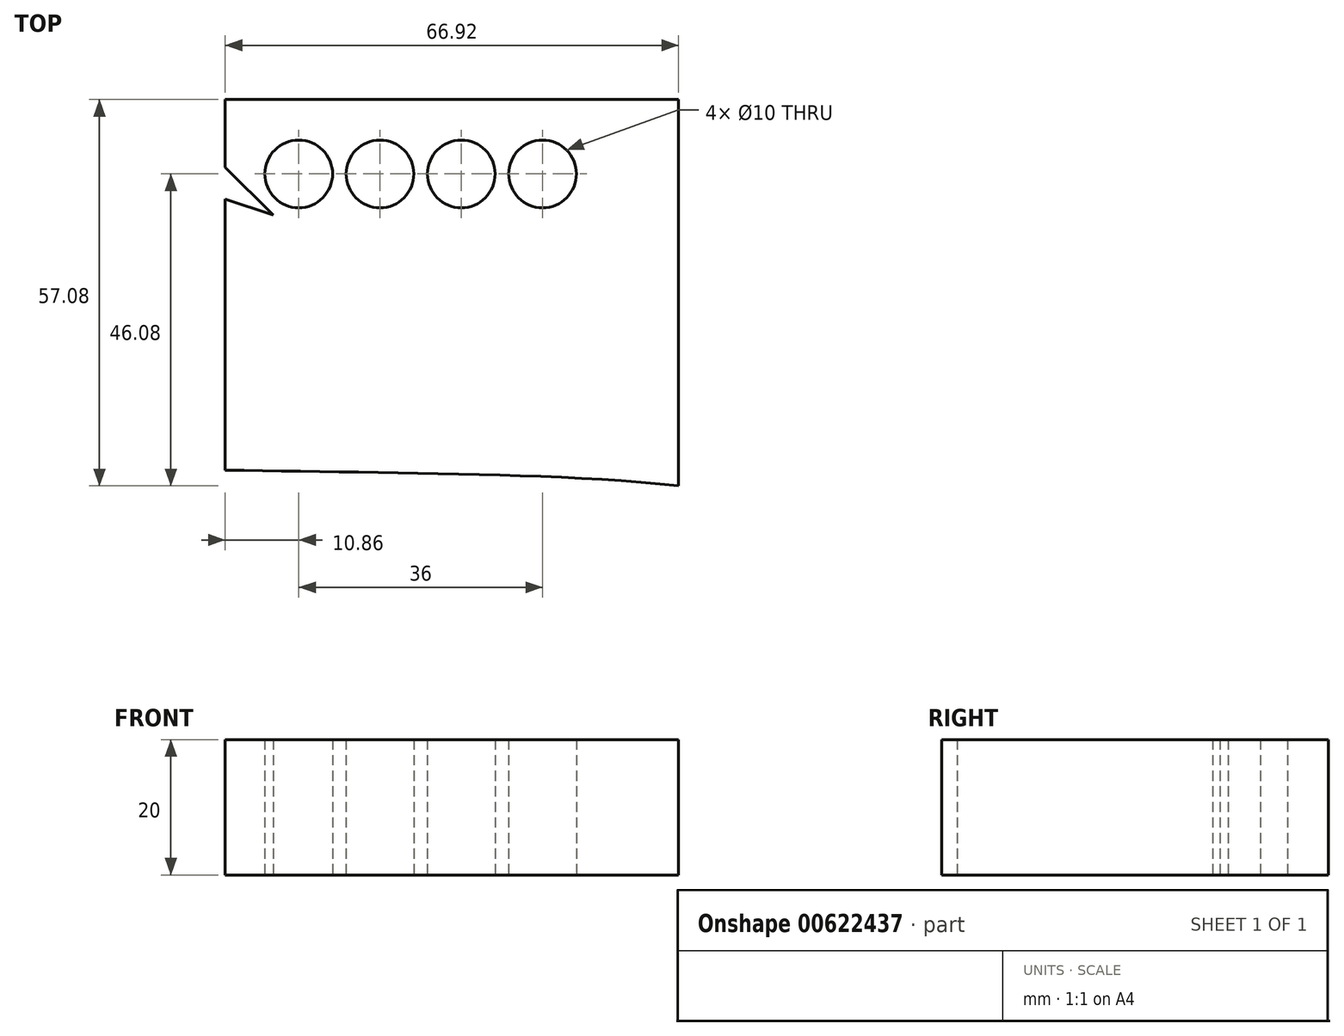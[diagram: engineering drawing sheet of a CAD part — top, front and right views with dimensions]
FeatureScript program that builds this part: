
annotation { "Feature Type Name" : "Feature", "Feature Type Description" : "" }
export const myFeature = defineFeature(function(context is Context, id is Id, definition is map)
    precondition{}
    {
        {
            var Q0;
            Q0=qCreatedBy(makeId("Top.planeOp"),FACE);
            var sketch = newSketch(context, id + "F0", { "sketchPlane" : qUnion([Q0])});
            skLineSegment(sketch, "E0", {"start": v(0, 0) * mm, "end": v(-230.94, 0) * mm});
            skLineSegment(sketch, "E1", {"start": v(-230.94, 0) * mm, "end": v(219.06, 0) * mm});
            skLineSegment(sketch, "E2", {"start": v(-178.77, 83.87) * mm, "end": v(166.23, 83.87) * mm});
            skLineSegment(sketch, "E3", {"start": v(-179.55, -84.3) * mm, "end": v(165.45, -84.3) * mm});
            skFitSpline(sketch, "E4", {"points": [v(-178.77, 83.87) * mm, v(-187.34, 83.87) * mm, v(-196.05, 82.03) * mm, v(-204.13, 75.85) * mm, v(-210.77, 67.6) * mm, v(-219.63, 55.04) * mm, v(-230.94, 0) * mm], "startDerivative": vector(-62.46, 1.75) * mm, "endDerivative": vector(-42.93, -222.96) * mm});
            skFitSpline(sketch, "E5", {"points": [v(-179.55, -84.3) * mm, v(-186, -84.3) * mm, v(-194.36, -82.98) * mm, v(-205.47, -75.53) * mm, v(-213.5, -67.51) * mm, v(-220.85, -55.02) * mm, v(-230.94, 0) * mm], "startDerivative": vector(-58.45, -0.77) * mm, "endDerivative": vector(-25.53, 220.68) * mm});
            skFitSpline(sketch, "E6", {"points": [v(79.72, -68.87) * mm, v(94.3, -68.2) * mm, v(121.52, -65.29) * mm, v(156.84, -57.83) * mm, v(194.43, -52) * mm, v(219.05, -51.68) * mm], "startDerivative": vector(92.48, 2.44) * mm, "endDerivative": vector(217.99, 5.07) * mm});
            skFitSpline(sketch, "E7.MirrorCS", {"points": [v(79.72, 68.87) * mm, v(94.3, 68.2) * mm, v(121.52, 65.29) * mm, v(156.84, 57.83) * mm, v(194.43, 52) * mm, v(219.05, 51.68) * mm], "startDerivative": vector(92.48, -2.44) * mm, "endDerivative": vector(217.99, -5.07) * mm});
            skLineSegment(sketch, "E8", {"start": v(219.05, -51.68) * mm, "end": v(219.05, 51.68) * mm});
            skFitSpline(sketch, "E9", {"points": [v(79.72, 68.87) * mm, v(56.8, 68.87) * mm, v(17.56, 68.87) * mm, v(-22.6, 68.87) * mm, v(-58.57, 65.44) * mm, v(-84.69, 58.45) * mm, v(-132, 55.24) * mm, v(-177.02, 54.67) * mm, v(-219.63, 55.04) * mm], "startDerivative": vector(-222.73, 0.47) * mm, "endDerivative": vector(-322.68, 5.5) * mm});
            skFitSpline(sketch, "E10.MirrorCS", {"points": [v(79.72, -68.87) * mm, v(56.8, -68.87) * mm, v(17.56, -68.87) * mm, v(-22.6, -68.87) * mm, v(-58.57, -65.44) * mm, v(-84.69, -58.45) * mm, v(-132, -55.24) * mm, v(-177.02, -54.67) * mm, v(-219.63, -55.04) * mm], "startDerivative": vector(-222.73, -0.47) * mm, "endDerivative": vector(-322.68, -5.5) * mm});
            skCircle(sketch, "E11", {"center": v(-150, 11) * mm, "radius": 5 * mm});
            skCircle(sketch, "E12", {"center": v(-138, 11) * mm, "radius": 5 * mm});
            skCircle(sketch, "E13", {"center": v(-126, 11) * mm, "radius": 5 * mm});
            skCircle(sketch, "E14", {"center": v(-114, 11) * mm, "radius": 5 * mm});
            skCircle(sketch, "E15.MirrorC", {"center": v(-150, -11) * mm, "radius": 5 * mm});
            skCircle(sketch, "E16.MirrorC", {"center": v(-138, -11) * mm, "radius": 5 * mm});
            skCircle(sketch, "E17.MirrorC", {"center": v(-126, -11) * mm, "radius": 5 * mm});
            skCircle(sketch, "E18.MirrorC", {"center": v(-114, -11) * mm, "radius": 5 * mm});
            skFitSpline(sketch, "E19", {"points": [v(-225.2, 0) * mm, v(-222.12, 3.4) * mm, v(-216.92, 6.48) * mm, v(-200.74, 8.98) * mm, v(-175.64, 9.89) * mm, v(-160.86, 10) * mm], "startDerivative": vector(24.07, 28.7) * mm, "endDerivative": vector(83.9, -2.27) * mm});
            skFitSpline(sketch, "E20.MirrorCS", {"points": [v(-225.2, 0) * mm, v(-222.12, -3.4) * mm, v(-216.92, -6.48) * mm, v(-200.74, -8.98) * mm, v(-175.64, -9.89) * mm, v(-160.86, -10) * mm], "startDerivative": vector(24.07, -28.7) * mm, "endDerivative": vector(83.9, 2.27) * mm});
            skLineSegment(sketch, "E21", {"start": v(-160.86, 10) * mm, "end": v(-153.79, 17.07) * mm});
            skLineSegment(sketch, "E22", {"start": v(-153.79, 17.07) * mm, "end": v(-175.64, 9.89) * mm});
            skLineSegment(sketch, "E23.MirrorCS", {"start": v(-153.79, -17.07) * mm, "end": v(-175.64, -9.89) * mm});
            skLineSegment(sketch, "E24.MirrorCS", {"start": v(-160.86, -10) * mm, "end": v(-153.79, -17.07) * mm});
            skLineSegment(sketch, "E25", {"start": v(-160.86, -10) * mm, "end": v(-160.86, 10) * mm});
            skFitSpline(sketch, "E26", {"points": [v(-178.77, 83.87) * mm, v(-169.02, 82.7) * mm, v(-159.87, 79.14) * mm, v(-148.12, 75.77) * mm, v(-129.24, 75.28) * mm, v(-93.94, 75.39) * mm, v(-67.97, 75) * mm], "startDerivative": vector(81.86, -4.03) * mm, "endDerivative": vector(119.84, 0.08) * mm});
            skFitSpline(sketch, "E27.MirrorCS", {"points": [v(-178.77, -83.87) * mm, v(-169.02, -82.7) * mm, v(-159.87, -79.14) * mm, v(-148.12, -75.77) * mm, v(-129.24, -75.28) * mm, v(-93.94, -75.39) * mm, v(-67.97, -75) * mm], "startDerivative": vector(81.86, 4.03) * mm, "endDerivative": vector(119.84, -0.08) * mm});
            skLineSegment(sketch, "E28", {"start": v(-67.97, -75) * mm, "end": v(-67.97, 75) * mm});
            skFitSpline(sketch, "E29", {"points": [v(-67.97, 0) * mm, v(-67.5, 28.25) * mm, v(-62.4, 57.87) * mm, v(-58.57, 65.44) * mm], "startDerivative": vector(-1.44, 69.17) * mm, "endDerivative": vector(18.48, 28.28) * mm});
            skFitSpline(sketch, "E30", {"points": [v(-27.72, 0) * mm, v(-27.53, 10.1) * mm, v(-26.76, 22.8) * mm, v(-25.02, 37.64) * mm, v(-22.93, 50.89) * mm, v(-23.45, 53.52) * mm, v(-24.88, 55.43) * mm, v(-31.62, 58.29) * mm, v(-44.77, 62.44) * mm, v(-53.63, 64.9) * mm, v(-58.57, 65.44) * mm], "startDerivative": vector(0.96, 90.1) * mm, "endDerivative": vector(-71.13, -5.45) * mm});
            skFitSpline(sketch, "E31.MirrorCS", {"points": [v(-67.97, 0) * mm, v(-67.5, -28.25) * mm, v(-62.4, -57.87) * mm, v(-58.57, -65.44) * mm], "startDerivative": vector(-1.44, -69.17) * mm, "endDerivative": vector(18.48, -28.28) * mm});
            skFitSpline(sketch, "E32.MirrorCS", {"points": [v(-27.72, 0) * mm, v(-27.53, -10.1) * mm, v(-26.76, -22.8) * mm, v(-25.02, -37.64) * mm, v(-22.93, -50.89) * mm, v(-23.45, -53.52) * mm, v(-24.88, -55.43) * mm, v(-31.62, -58.29) * mm, v(-44.77, -62.44) * mm, v(-53.63, -64.9) * mm, v(-58.57, -65.44) * mm], "startDerivative": vector(0.96, -90.1) * mm, "endDerivative": vector(-71.13, 5.45) * mm});
            skFitSpline(sketch, "E33", {"points": [v(-62.75, -84.3) * mm, v(-60.8, -79.88) * mm, v(-55.46, -75.02) * mm, v(-52.87, -70.97) * mm, v(-40.55, -66.27) * mm, v(-28.56, -61.4) * mm, v(-19.17, -57.84) * mm, v(-7.66, -56.87) * mm, v(38.5, -57.03) * mm, v(48.88, -57.03) * mm, v(52.93, -58.33) * mm, v(53.58, -61.57) * mm, v(53.58, -65.46) * mm, v(56.8, -68.87) * mm, v(58.76, -71.78) * mm, v(59.08, -75.02) * mm, v(60.22, -78.58) * mm, v(61.35, -81.5) * mm, v(61.68, -84.3) * mm], "startDerivative": vector(25.17, 99.57) * mm, "endDerivative": vector(3.97, -81.05) * mm});
            skFitSpline(sketch, "E34.MirrorCS", {"points": [v(-62.75, 84.3) * mm, v(-60.8, 79.88) * mm, v(-55.46, 75.02) * mm, v(-52.87, 70.97) * mm, v(-40.55, 66.27) * mm, v(-28.56, 61.4) * mm, v(-19.17, 57.84) * mm, v(-7.66, 56.87) * mm, v(38.5, 57.03) * mm, v(48.88, 57.03) * mm, v(52.93, 58.33) * mm, v(53.58, 61.57) * mm, v(53.58, 65.46) * mm, v(56.8, 68.87) * mm, v(58.76, 71.78) * mm, v(59.08, 75.02) * mm, v(60.22, 78.58) * mm, v(61.35, 81.5) * mm, v(61.68, 84.3) * mm], "startDerivative": vector(25.17, -99.57) * mm, "endDerivative": vector(3.97, 81.05) * mm});
            skFitSpline(sketch, "E35", {"points": [v(-24.88, -55.43) * mm, v(-12.02, -53.52) * mm, v(6.86, -53.52) * mm, v(37.1, -53.52) * mm, v(83.73, -53.52) * mm, v(146.25, -52.5) * mm, v(194.43, -52) * mm], "startDerivative": vector(120.5, 23.1) * mm, "endDerivative": vector(233.25, 1.68) * mm});
            skFitSpline(sketch, "E36.MirrorCS", {"points": [v(-24.88, 55.43) * mm, v(-12.02, 53.52) * mm, v(6.86, 53.52) * mm, v(37.1, 53.52) * mm, v(83.73, 53.52) * mm, v(146.25, 52.5) * mm, v(194.43, 52) * mm], "startDerivative": vector(120.5, -23.1) * mm, "endDerivative": vector(233.25, -1.68) * mm});
            skFitSpline(sketch, "E37", {"points": [v(-178.77, 83.87) * mm, v(-173.62, 87.43) * mm, v(-167.64, 90.13) * mm, v(-150.69, 91.48) * mm, v(-129.69, 91.48) * mm, v(-115.05, 90.7) * mm, v(-105.41, 88.2) * mm, v(-79.02, 83.87) * mm], "startDerivative": vector(56.5, 37.37) * mm, "endDerivative": vector(150.4, -20.43) * mm});
            skFitSpline(sketch, "E38.MirrorCS", {"points": [v(-178.77, -83.87) * mm, v(-173.62, -87.43) * mm, v(-167.64, -90.13) * mm, v(-150.69, -91.48) * mm, v(-129.69, -91.48) * mm, v(-115.05, -90.7) * mm, v(-105.41, -88.2) * mm, v(-79.02, -83.87) * mm], "startDerivative": vector(56.5, -37.37) * mm, "endDerivative": vector(150.4, 20.43) * mm});
            skLineSegment(sketch, "E39", {"start": v(80.91, 83.87) * mm, "end": v(97.5, 92.07) * mm});
            skLineSegment(sketch, "E40", {"start": v(97.5, 92.07) * mm, "end": v(152.5, 92.07) * mm});
            skLineSegment(sketch, "E41", {"start": v(152.5, 92.07) * mm, "end": v(166.23, 83.87) * mm});
            skLineSegment(sketch, "E42.MirrorCS", {"start": v(97.5, -92.07) * mm, "end": v(152.5, -92.07) * mm});
            skLineSegment(sketch, "E43.MirrorCS", {"start": v(80.91, -83.87) * mm, "end": v(97.5, -92.07) * mm});
            skLineSegment(sketch, "E44.MirrorCS", {"start": v(152.5, -92.07) * mm, "end": v(166.23, -83.87) * mm});
            skFitSpline(sketch, "E45", {"points": [v(166.23, 83.87) * mm, v(184.2, 83.23) * mm, v(201.93, 81.2) * mm, v(213.5, 79.09) * mm, v(217.73, 76) * mm, v(219.05, 66.66) * mm, v(219.05, 51.68) * mm], "startDerivative": vector(85.73, -5.93) * mm, "endDerivative": vector(1.13, -79.24) * mm});
            skFitSpline(sketch, "E46.MirrorCS", {"points": [v(166.23, -83.87) * mm, v(184.2, -83.23) * mm, v(201.93, -81.2) * mm, v(213.5, -79.09) * mm, v(217.73, -76) * mm, v(219.05, -66.66) * mm, v(219.05, -51.68) * mm], "startDerivative": vector(85.73, 5.93) * mm, "endDerivative": vector(1.13, 79.24) * mm});
            skLineSegment(sketch, "E47", {"start": v(86.33, -46) * mm, "end": v(86.33, 46) * mm});
            skLineSegment(sketch, "E48.bottom", {"start": v(162.94, -49) * mm, "end": v(95.88, -49) * mm});
            skLineSegment(sketch, "E48.top", {"start": v(162.94, 49) * mm, "end": v(95.88, 49) * mm});
            skLineSegment(sketch, "E48.left", {"start": v(162.94, -49) * mm, "end": v(162.94, 49) * mm});
            skLineSegment(sketch, "E48.right", {"start": v(90.88, -44) * mm, "end": v(90.88, 44) * mm});
            skArc(sketch, "E49.filletArc", {"start": v(95.88, 49) * mm, "mid": v(92.35, 47.54) * mm, "end": v(90.88, 44) * mm});
            skArc(sketch, "E50.filletArc", {"start": v(90.88, -44) * mm, "mid": v(92.35, -47.54) * mm, "end": v(95.88, -49) * mm});
            skFitSpline(sketch, "E51", {"points": [v(86.33, 46) * mm, v(87.19, 48.66) * mm, v(89.37, 51.17) * mm, v(92.2, 52.55) * mm, v(113.19, 53.1) * mm], "startDerivative": vector(3.3, 15.9) * mm, "endDerivative": vector(55.9, -0.73) * mm});
            skFitSpline(sketch, "E52.MirrorCS", {"points": [v(86.33, -46) * mm, v(87.19, -48.66) * mm, v(89.37, -51.17) * mm, v(92.2, -52.55) * mm, v(113.19, -53.1) * mm], "startDerivative": vector(3.3, -15.9) * mm, "endDerivative": vector(55.9, 0.73) * mm});
            skLineSegment(sketch, "E53", {"start": v(-93.94, 57.08) * mm, "end": v(-93.94, -57.08) * mm});
            skLineSegment(sketch, "E54", {"start": v(-160.86, 0) * mm, "end": v(-160.86, -91.09) * mm});
            skLineSegment(sketch, "E55", {"start": v(-160.86, -91.09) * mm, "end": v(-160.86, 91.09) * mm});
            skSolve(sketch);
        }
        {
            var Q0;
            Q0=makeQuery(id+"F0.imprint","IMPRINT",FACE,{"disambiguationData":[TD([[makeQuery(id+"F0.imprint","IMPRINT",EDGE,{"derivedFrom":sQuery(id+"F0.wireOp",EDGE,"E15.MirrorC")}),-1.0]])]});
            var Q1;
            Q1=makeQuery(id+"F0.imprint","IMPRINT",FACE,{"disambiguationData":[TD([[makeQuery(id+"F0.imprint","IMPRINT",EDGE,{"derivedFrom":sQuery(id+"F0.wireOp",EDGE,"E17.MirrorC")}),-1.0]])]});
            var Q2;
            Q2=makeQuery(id+"F0.imprint","IMPRINT",FACE,{"disambiguationData":[TD([[makeQuery(id+"F0.imprint","IMPRINT",EDGE,{"derivedFrom":sQuery(id+"F0.wireOp",EDGE,"E18.MirrorC")}),-1.0]])]});
            var Q3;
            Q3=makeQuery(id+"F0.imprint","IMPRINT",FACE,{"disambiguationData":[TD([[makeQuery(id+"F0.imprint","IMPRINT",EDGE,{"derivedFrom":sQuery(id+"F0.wireOp",EDGE,"E16.MirrorC")}),-1.0]])]});
            extrude(context, id + "F1", {"entities" : qUnion([Q0, Q1, Q2, Q3]), "depth" : 20 * mm, "offsetDistance" : 25 * mm});
        }
        {
            var Q0;
            Q0=sQuery(id+"F0.wireOp",EDGE,"E5");
            extrude(context, id + "F2", {"bodyType" : ToolBodyType.SURFACE, "surfaceEntities" : qUnion([Q0]), "depth" : 25 * mm, "offsetDistance" : 25 * mm});
        }
    });
